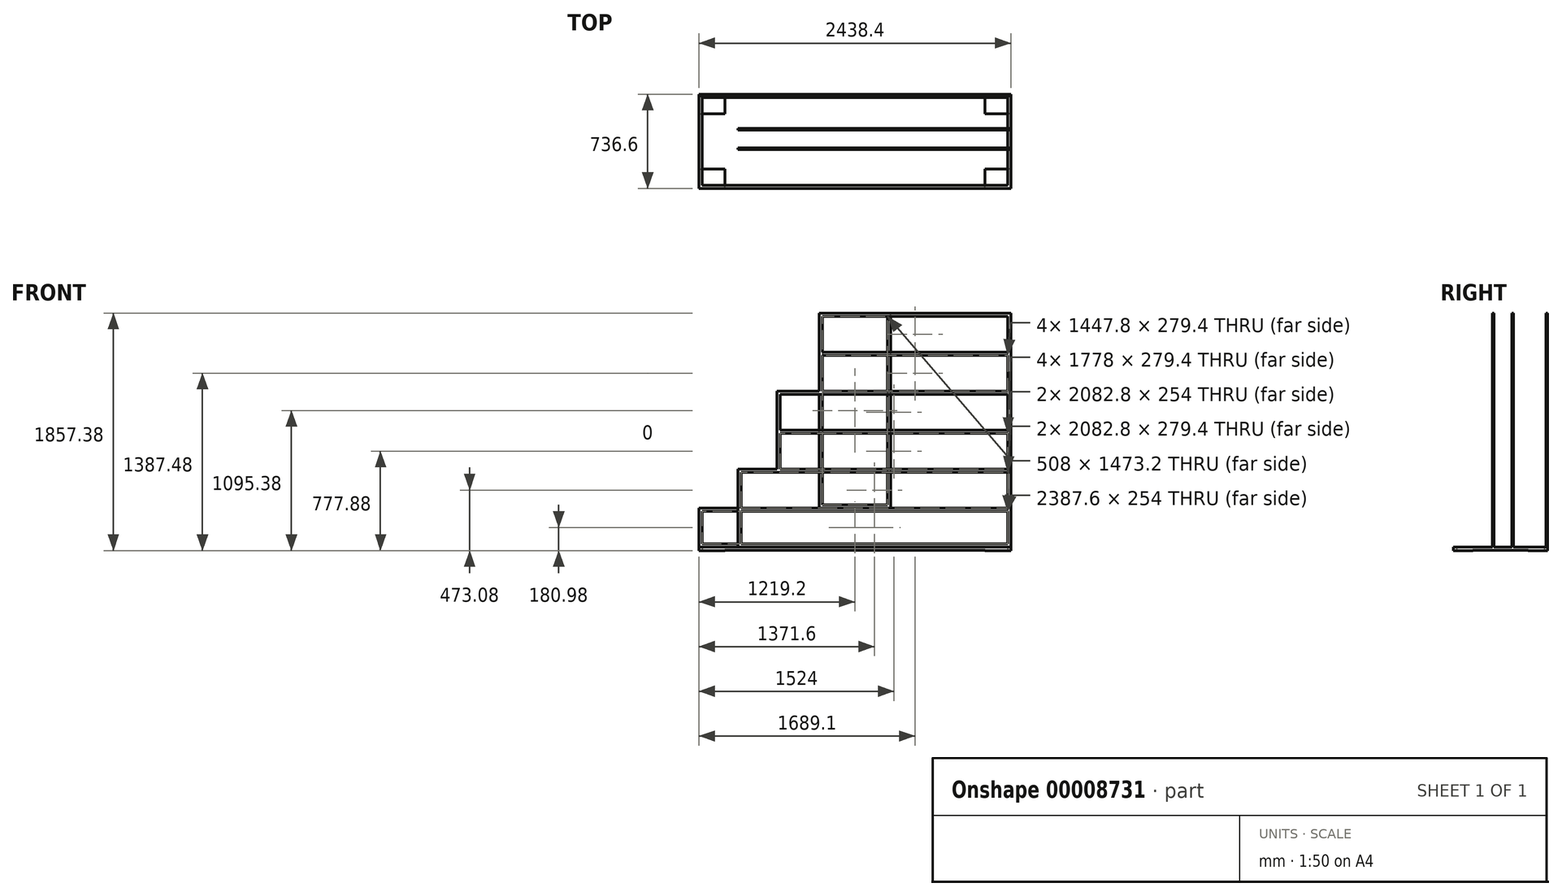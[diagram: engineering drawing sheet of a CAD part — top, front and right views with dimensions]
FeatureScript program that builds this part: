
annotation { "Feature Type Name" : "Feature", "Feature Type Description" : "" }
export const myFeature = defineFeature(function(context is Context, id is Id, definition is map)
    precondition{}
    {
        {
            var Q0;
            Q0=qCreatedBy(makeId("Top.planeOp"),FACE);
            var sketch = newSketch(context, id + "F0", { "sketchPlane" : qUnion([Q0])});
            skLineSegment(sketch, "E0.bottom", {"start": v(0, 0) * mm, "end": v(-2438.4, 0) * mm});
            skLineSegment(sketch, "E0.top", {"start": v(0, -736.6) * mm, "end": v(-2438.4, -736.6) * mm});
            skLineSegment(sketch, "E0.left", {"start": v(0, 0) * mm, "end": v(0, -736.6) * mm});
            skLineSegment(sketch, "E0.right", {"start": v(-2438.4, 0) * mm, "end": v(-2438.4, -736.6) * mm});
            skLineSegment(sketch, "E1.bottom", {"start": v(-25.4, -25.4) * mm, "end": v(-2413, -25.4) * mm});
            skLineSegment(sketch, "E1.top", {"start": v(-25.4, -711.2) * mm, "end": v(-2413, -711.2) * mm});
            skLineSegment(sketch, "E1.left", {"start": v(-25.4, -25.4) * mm, "end": v(-25.4, -711.2) * mm});
            skLineSegment(sketch, "E1.right", {"start": v(-2413, -25.4) * mm, "end": v(-2413, -711.2) * mm});
            skLineSegment(sketch, "E2.bottom", {"start": v(-2235.2, -25.4) * mm, "end": v(-2260.6, -25.4) * mm});
            skLineSegment(sketch, "E2.top", {"start": v(-2235.2, -711.2) * mm, "end": v(-2260.6, -711.2) * mm});
            skLineSegment(sketch, "E2.left", {"start": v(-2235.2, -25.4) * mm, "end": v(-2235.2, -711.2) * mm});
            skLineSegment(sketch, "E2.right", {"start": v(-2260.6, -25.4) * mm, "end": v(-2260.6, -711.2) * mm});
            skLineSegment(sketch, "E3.bottom", {"start": v(-203.2, -25.4) * mm, "end": v(-177.8, -25.4) * mm});
            skLineSegment(sketch, "E3.top", {"start": v(-203.2, -711.2) * mm, "end": v(-177.8, -711.2) * mm});
            skLineSegment(sketch, "E3.left", {"start": v(-203.2, -25.4) * mm, "end": v(-203.2, -711.2) * mm});
            skLineSegment(sketch, "E3.right", {"start": v(-177.8, -25.4) * mm, "end": v(-177.8, -711.2) * mm});
            skLineSegment(sketch, "E4.bottom", {"start": v(-1625.6, -25.4) * mm, "end": v(-1600.2, -25.4) * mm});
            skLineSegment(sketch, "E4.top", {"start": v(-1625.6, -711.2) * mm, "end": v(-1600.2, -711.2) * mm});
            skLineSegment(sketch, "E5.bottom", {"start": v(-1168.4, -25.4) * mm, "end": v(-1143, -25.4) * mm});
            skLineSegment(sketch, "E5.top", {"start": v(-1168.4, -711.2) * mm, "end": v(-1143, -711.2) * mm});
            skLineSegment(sketch, "E6.bottom", {"start": v(-838.2, -25.4) * mm, "end": v(-812.8, -25.4) * mm});
            skLineSegment(sketch, "E6.top", {"start": v(-838.2, -711.2) * mm, "end": v(-812.8, -711.2) * mm});
            skLineSegment(sketch, "E7.bottom", {"start": v(-1816.1, -25.4) * mm, "end": v(-1841.5, -25.4) * mm});
            skLineSegment(sketch, "E7.top", {"start": v(-1816.1, -711.2) * mm, "end": v(-1841.5, -711.2) * mm});
            skLineSegment(sketch, "E7.left", {"start": v(-1816.1, -25.4) * mm, "end": v(-1816.1, -711.2) * mm});
            skLineSegment(sketch, "E7.right", {"start": v(-1841.5, -25.4) * mm, "end": v(-1841.5, -711.2) * mm});
            skLineSegment(sketch, "E8.bottom", {"start": v(-1435.1, -25.4) * mm, "end": v(-1409.7, -25.4) * mm});
            skLineSegment(sketch, "E8.top", {"start": v(-1435.1, -711.2) * mm, "end": v(-1409.7, -711.2) * mm});
            skLineSegment(sketch, "E8.left", {"start": v(-1435.1, -25.4) * mm, "end": v(-1435.1, -711.2) * mm});
            skLineSegment(sketch, "E8.right", {"start": v(-1409.7, -25.4) * mm, "end": v(-1409.7, -711.2) * mm});
            skLineSegment(sketch, "E9.bottom", {"start": v(-1028.7, -25.4) * mm, "end": v(-1003.3, -25.4) * mm});
            skLineSegment(sketch, "E9.top", {"start": v(-1028.7, -711.2) * mm, "end": v(-1003.3, -711.2) * mm});
            skLineSegment(sketch, "E9.left", {"start": v(-1028.7, -25.4) * mm, "end": v(-1028.7, -711.2) * mm});
            skLineSegment(sketch, "E9.right", {"start": v(-1003.3, -25.4) * mm, "end": v(-1003.3, -711.2) * mm});
            skLineSegment(sketch, "E10.bottom", {"start": v(-622.3, -25.4) * mm, "end": v(-596.9, -25.4) * mm});
            skLineSegment(sketch, "E10.top", {"start": v(-622.3, -711.2) * mm, "end": v(-596.9, -711.2) * mm});
            skLineSegment(sketch, "E10.left", {"start": v(-622.3, -25.4) * mm, "end": v(-622.3, -711.2) * mm});
            skLineSegment(sketch, "E10.right", {"start": v(-596.9, -25.4) * mm, "end": v(-596.9, -711.2) * mm});
            skSolve(sketch);
        }
        {
            var Q0;
            Q0 = qSketchRegion(id + "F0", true);
            var Q1;
            Q1=makeQuery(id+"F0.imprint","IMPRINT",FACE,{"disambiguationData":[TD([[makeQuery(id+"F0.imprint","IMPRINT",EDGE,{"derivedFrom":sQuery(id+"F0.wireOp",EDGE,"E2.bottom")}),1.0]])]});
            var Q2;
            Q2=makeQuery(id+"F0.imprint","IMPRINT",FACE,{"disambiguationData":[TD([[makeQuery(id+"F0.imprint","IMPRINT",EDGE,{"derivedFrom":sQuery(id+"F0.wireOp",EDGE,"E7.bottom")}),1.0]])]});
            var Q3;
            Q3=makeQuery(id+"F0.imprint","IMPRINT",FACE,{"disambiguationData":[TD([[makeQuery(id+"F0.imprint","IMPRINT",EDGE,{"derivedFrom":sQuery(id+"F0.wireOp",EDGE,"E8.bottom")}),-1.0]])]});
            var Q4;
            Q4=makeQuery(id+"F0.imprint","IMPRINT",FACE,{"disambiguationData":[TD([[makeQuery(id+"F0.imprint","IMPRINT",EDGE,{"derivedFrom":sQuery(id+"F0.wireOp",EDGE,"E9.bottom")}),-1.0]])]});
            var Q5;
            Q5=makeQuery(id+"F0.imprint","IMPRINT",FACE,{"disambiguationData":[TD([[makeQuery(id+"F0.imprint","IMPRINT",EDGE,{"derivedFrom":sQuery(id+"F0.wireOp",EDGE,"E10.bottom")}),-1.0]])]});
            var Q6;
            Q6=makeQuery(id+"F0.imprint","IMPRINT",FACE,{"disambiguationData":[TD([[makeQuery(id+"F0.imprint","IMPRINT",EDGE,{"derivedFrom":sQuery(id+"F0.wireOp",EDGE,"E3.bottom")}),-1.0]])]});
            extrude(context, id + "F1", {"entities" : qUnion([Q0, Q1, Q2, Q3, Q4, Q5, Q6]), "depth" : 25.4 * mm});
        }
        {
            var Q0;
            Q0=makeQuery(id+"F1.opExtrude","CAP_FACE",FACE,{"disambiguationData":[OSD([sQuery(id+"F0.wireOp",EDGE,"E0.bottom"),sQuery(id+"F0.wireOp",EDGE,"E0.top"),sQuery(id+"F0.wireOp",EDGE,"E0.left"),sQuery(id+"F0.wireOp",EDGE,"E0.right"),sQuery(id+"F0.wireOp",EDGE,"E1.bottom"),sQuery(id+"F0.wireOp",EDGE,"E1.top"),sQuery(id+"F0.wireOp",EDGE,"E1.left"),sQuery(id+"F0.wireOp",EDGE,"E1.right"),sQuery(id+"F0.wireOp",EDGE,"E2.left"),sQuery(id+"F0.wireOp",EDGE,"E2.right"),sQuery(id+"F0.wireOp",EDGE,"E3.left"),sQuery(id+"F0.wireOp",EDGE,"E3.right"),sQuery(id+"F0.wireOp",EDGE,"E4.bottom"),sQuery(id+"F0.wireOp",EDGE,"E4.top"),sQuery(id+"F0.wireOp",EDGE,"E5.bottom"),sQuery(id+"F0.wireOp",EDGE,"E5.top"),sQuery(id+"F0.wireOp",EDGE,"E6.bottom"),sQuery(id+"F0.wireOp",EDGE,"E6.top"),sQuery(id+"F0.wireOp",EDGE,"E7.left"),sQuery(id+"F0.wireOp",EDGE,"E7.right"),sQuery(id+"F0.wireOp",EDGE,"E8.left"),sQuery(id+"F0.wireOp",EDGE,"E8.right"),sQuery(id+"F0.wireOp",EDGE,"E9.left"),sQuery(id+"F0.wireOp",EDGE,"E9.right"),sQuery(id+"F0.wireOp",EDGE,"E10.left"),sQuery(id+"F0.wireOp",EDGE,"E10.right")])],"isStart":true});
            var sketch = newSketch(context, id + "F2", { "sketchPlane" : qUnion([Q0])});
            skLineSegment(sketch, "E11.bottom", {"start": v(-2438.4, 736.6) * mm, "end": v(-2235.2, 736.6) * mm});
            skLineSegment(sketch, "E11.top", {"start": v(-2438.4, 584.2) * mm, "end": v(-2235.2, 584.2) * mm});
            skLineSegment(sketch, "E11.left", {"start": v(-2438.4, 736.6) * mm, "end": v(-2438.4, 584.2) * mm});
            skLineSegment(sketch, "E11.right", {"start": v(-2235.2, 736.6) * mm, "end": v(-2235.2, 584.2) * mm});
            skLineSegment(sketch, "E12.bottom", {"start": v(-2438.4, 0) * mm, "end": v(-2235.2, 0) * mm});
            skLineSegment(sketch, "E12.top", {"start": v(-2438.4, 152.4) * mm, "end": v(-2235.2, 152.4) * mm});
            skLineSegment(sketch, "E12.left", {"start": v(-2438.4, 0) * mm, "end": v(-2438.4, 152.4) * mm});
            skLineSegment(sketch, "E12.right", {"start": v(-2235.2, 0) * mm, "end": v(-2235.2, 152.4) * mm});
            skLineSegment(sketch, "E13.bottom", {"start": v(0, 736.6) * mm, "end": v(-203.2, 736.6) * mm});
            skLineSegment(sketch, "E13.top", {"start": v(0, 584.2) * mm, "end": v(-203.2, 584.2) * mm});
            skLineSegment(sketch, "E13.left", {"start": v(0, 736.6) * mm, "end": v(0, 584.2) * mm});
            skLineSegment(sketch, "E13.right", {"start": v(-203.2, 736.6) * mm, "end": v(-203.2, 584.2) * mm});
            skLineSegment(sketch, "E14.bottom", {"start": v(0, 0) * mm, "end": v(-203.2, 0) * mm});
            skLineSegment(sketch, "E14.top", {"start": v(0, 152.4) * mm, "end": v(-203.2, 152.4) * mm});
            skLineSegment(sketch, "E14.left", {"start": v(0, 0) * mm, "end": v(0, 152.4) * mm});
            skLineSegment(sketch, "E14.right", {"start": v(-203.2, 0) * mm, "end": v(-203.2, 152.4) * mm});
            skSolve(sketch);
        }
        {
            var Q0;
            Q0 = qSketchRegion(id + "F2", true);
            extrude(context, id + "F3", {"entities" : qUnion([Q0]), "operationType" : NewBodyOperationType.ADD, "depth" : 3.17 * mm});
        }
        {
            var Q0;
            Q0=makeQuery(id+"F3.boolean.opBoolean","MERGE",FACE,{"derivedFrom":[makeQuery(id+"F1.opExtrude","SWEPT_FACE",FACE,{"disambiguationData":[OSD([sQuery(id+"F0.wireOp",EDGE,"E0.bottom")])]}),makeQuery(id+"F3.opExtrude","SWEPT_FACE",FACE,{"disambiguationData":[OSD([sQuery(id+"F2.wireOp",EDGE,"E12.bottom")])]}),makeQuery(id+"F3.opExtrude","SWEPT_FACE",FACE,{"disambiguationData":[OSD([sQuery(id+"F2.wireOp",EDGE,"E14.bottom")])]})]});
            var sketch = newSketch(context, id + "F4", { "sketchPlane" : qUnion([Q0])});
            skLineSegment(sketch, "E15.bottom", {"start": v(0, 25.4) * mm, "end": v(2438.4, 25.4) * mm});
            skLineSegment(sketch, "E15.top", {"start": v(0, 330.2) * mm, "end": v(2438.4, 330.2) * mm});
            skLineSegment(sketch, "E15.left", {"start": v(0, 25.4) * mm, "end": v(0, 330.2) * mm});
            skLineSegment(sketch, "E15.right", {"start": v(2438.4, 25.4) * mm, "end": v(2438.4, 330.2) * mm});
            skLineSegment(sketch, "E16.bottom", {"start": v(939.8, 330.2) * mm, "end": v(1498.6, 330.2) * mm});
            skLineSegment(sketch, "E16.top", {"start": v(939.8, 1854.2) * mm, "end": v(1498.6, 1854.2) * mm});
            skLineSegment(sketch, "E16.left", {"start": v(939.8, 330.2) * mm, "end": v(939.8, 1854.2) * mm});
            skLineSegment(sketch, "E16.right", {"start": v(1498.6, 330.2) * mm, "end": v(1498.6, 1854.2) * mm});
            skLineSegment(sketch, "E17.bottom", {"start": v(965.2, 1828.8) * mm, "end": v(1473.2, 1828.8) * mm});
            skLineSegment(sketch, "E17.top", {"start": v(965.2, 355.6) * mm, "end": v(1473.2, 355.6) * mm});
            skLineSegment(sketch, "E17.left", {"start": v(965.2, 1828.8) * mm, "end": v(965.2, 355.6) * mm});
            skLineSegment(sketch, "E17.right", {"start": v(1473.2, 1828.8) * mm, "end": v(1473.2, 355.6) * mm});
            skLineSegment(sketch, "E18.bottom", {"start": v(25.4, 304.8) * mm, "end": v(2413, 304.8) * mm});
            skLineSegment(sketch, "E18.top", {"start": v(25.4, 50.8) * mm, "end": v(2413, 50.8) * mm});
            skLineSegment(sketch, "E18.left", {"start": v(25.4, 304.8) * mm, "end": v(25.4, 50.8) * mm});
            skLineSegment(sketch, "E18.right", {"start": v(2413, 304.8) * mm, "end": v(2413, 50.8) * mm});
            skLineSegment(sketch, "E19.bottom", {"start": v(635, 304.8) * mm, "end": v(660.4, 304.8) * mm});
            skLineSegment(sketch, "E19.top", {"start": v(635, 50.8) * mm, "end": v(660.4, 50.8) * mm});
            skLineSegment(sketch, "E19.left", {"start": v(635, 304.8) * mm, "end": v(635, 50.8) * mm});
            skLineSegment(sketch, "E19.right", {"start": v(660.4, 304.8) * mm, "end": v(660.4, 50.8) * mm});
            skLineSegment(sketch, "E20.bottom", {"start": v(1778, 304.8) * mm, "end": v(1803.4, 304.8) * mm});
            skLineSegment(sketch, "E20.top", {"start": v(1778, 50.8) * mm, "end": v(1803.4, 50.8) * mm});
            skLineSegment(sketch, "E20.left", {"start": v(1778, 304.8) * mm, "end": v(1778, 50.8) * mm});
            skLineSegment(sketch, "E20.right", {"start": v(1803.4, 304.8) * mm, "end": v(1803.4, 50.8) * mm});
            skSolve(sketch);
        }
        {
            var Q0;
            Q0 = qSketchRegion(id + "F4", true);
            var Q1;
            Q1=makeQuery(id+"F4.imprint","IMPRINT",FACE,{"disambiguationData":[TD([[makeQuery(id+"F4.imprint","IMPRINT",EDGE,{"derivedFrom":sQuery(id+"F4.wireOp",EDGE,"E20.bottom")}),-1.0]])]});
            var Q2;
            Q2=makeQuery(id+"F4.imprint","IMPRINT",FACE,{"disambiguationData":[TD([[makeQuery(id+"F4.imprint","IMPRINT",EDGE,{"derivedFrom":sQuery(id+"F4.wireOp",EDGE,"E19.bottom")}),-1.0]])]});
            extrude(context, id + "F5", {"entities" : qUnion([Q0, Q1, Q2]), "oppositeDirection" : true, "depth" : 12.7 * mm});
        }
        {
            var Q0;
            Q0=makeQuery(id+"F5.opExtrude","CAP_FACE",FACE,{"disambiguationData":[OSD([sQuery(id+"F4.wireOp",EDGE,"E15.bottom"),sQuery(id+"F4.wireOp",EDGE,"E15.top"),sQuery(id+"F4.wireOp",EDGE,"E15.left"),sQuery(id+"F4.wireOp",EDGE,"E15.right"),sQuery(id+"F4.wireOp",EDGE,"E16.top"),sQuery(id+"F4.wireOp",EDGE,"E16.left"),sQuery(id+"F4.wireOp",EDGE,"E16.right"),sQuery(id+"F4.wireOp",EDGE,"E17.bottom"),sQuery(id+"F4.wireOp",EDGE,"E17.top"),sQuery(id+"F4.wireOp",EDGE,"E17.left"),sQuery(id+"F4.wireOp",EDGE,"E17.right"),sQuery(id+"F4.wireOp",EDGE,"E18.bottom"),sQuery(id+"F4.wireOp",EDGE,"E18.top"),sQuery(id+"F4.wireOp",EDGE,"E18.left"),sQuery(id+"F4.wireOp",EDGE,"E18.right"),sQuery(id+"F4.wireOp",EDGE,"E19.left"),sQuery(id+"F4.wireOp",EDGE,"E19.right"),sQuery(id+"F4.wireOp",EDGE,"E20.left"),sQuery(id+"F4.wireOp",EDGE,"E20.right")])],"isStart":false});
            cPlane(context, id + "F6", {"entities" : qUnion([Q0]), "cplaneType" : CPlaneType.OFFSET, "offset" : 254 * mm, "width" : 152.4 * mm, "height" : 152.4 * mm});
        }
        {
            var Q0;
            Q0=qCreatedBy(id+"F6.planeOp",FACE);
            var sketch = newSketch(context, id + "F7", { "sketchPlane" : qUnion([Q0])});
            skPoint(sketch, "E21.0", {"position": v(-2438.4, 25.4) * mm});
            skPoint(sketch, "E22.0", {"position": v(0, 25.4) * mm});
            skLineSegment(sketch, "E23.0", {"start": v(-939.8, 1854.2) * mm, "end": v(-1498.6, 1854.2) * mm});
            skLineSegment(sketch, "E24.bottom", {"start": v(0, 25.4) * mm, "end": v(-2133.6, 25.4) * mm});
            skLineSegment(sketch, "E24.top", {"start": v(0, 330.2) * mm, "end": v(-2133.6, 330.2) * mm});
            skLineSegment(sketch, "E24.left", {"start": v(0, 25.4) * mm, "end": v(0, 330.2) * mm});
            skLineSegment(sketch, "E24.right", {"start": v(-2133.6, 25.4) * mm, "end": v(-2133.6, 330.2) * mm});
            skLineSegment(sketch, "E25.top", {"start": v(0, 635) * mm, "end": v(-2133.6, 635) * mm});
            skLineSegment(sketch, "E25.left", {"start": v(0, 330.2) * mm, "end": v(0, 635) * mm});
            skLineSegment(sketch, "E25.right", {"start": v(-2133.6, 330.2) * mm, "end": v(-2133.6, 635) * mm});
            skLineSegment(sketch, "E26.bottom", {"start": v(0, 635) * mm, "end": v(-1828.8, 635) * mm});
            skLineSegment(sketch, "E26.top", {"start": v(0, 939.8) * mm, "end": v(-1828.8, 939.8) * mm});
            skLineSegment(sketch, "E26.left", {"start": v(0, 635) * mm, "end": v(0, 939.8) * mm});
            skLineSegment(sketch, "E26.right", {"start": v(-1828.8, 635) * mm, "end": v(-1828.8, 939.8) * mm});
            skLineSegment(sketch, "E27.top", {"start": v(0, 1244.6) * mm, "end": v(-1828.8, 1244.6) * mm});
            skLineSegment(sketch, "E27.left", {"start": v(0, 939.8) * mm, "end": v(0, 1244.6) * mm});
            skLineSegment(sketch, "E27.right", {"start": v(-1828.8, 939.8) * mm, "end": v(-1828.8, 1244.6) * mm});
            skLineSegment(sketch, "E28.bottom", {"start": v(0, 1244.6) * mm, "end": v(-1498.6, 1244.6) * mm});
            skLineSegment(sketch, "E28.top", {"start": v(0, 1549.4) * mm, "end": v(-1498.6, 1549.4) * mm});
            skLineSegment(sketch, "E28.left", {"start": v(0, 1244.6) * mm, "end": v(0, 1549.4) * mm});
            skLineSegment(sketch, "E28.right", {"start": v(-1498.6, 1244.6) * mm, "end": v(-1498.6, 1549.4) * mm});
            skLineSegment(sketch, "E29.top", {"start": v(0, 1854.2) * mm, "end": v(-1498.6, 1854.2) * mm});
            skLineSegment(sketch, "E29.left", {"start": v(0, 1549.4) * mm, "end": v(0, 1854.2) * mm});
            skLineSegment(sketch, "E29.right", {"start": v(-1498.6, 1549.4) * mm, "end": v(-1498.6, 1854.2) * mm});
            skLineSegment(sketch, "E30.bottom", {"start": v(-2108.2, 25.4) * mm, "end": v(-25.4, 25.4) * mm});
            skLineSegment(sketch, "E30.top", {"start": v(-2108.2, 304.8) * mm, "end": v(-25.4, 304.8) * mm});
            skLineSegment(sketch, "E30.left", {"start": v(-2108.2, 25.4) * mm, "end": v(-2108.2, 304.8) * mm});
            skLineSegment(sketch, "E30.right", {"start": v(-25.4, 25.4) * mm, "end": v(-25.4, 304.8) * mm});
            skLineSegment(sketch, "E31.bottom", {"start": v(-2108.2, 330.2) * mm, "end": v(-25.4, 330.2) * mm});
            skLineSegment(sketch, "E31.top", {"start": v(-2108.2, 609.6) * mm, "end": v(-25.4, 609.6) * mm});
            skLineSegment(sketch, "E31.left", {"start": v(-2108.2, 330.2) * mm, "end": v(-2108.2, 609.6) * mm});
            skLineSegment(sketch, "E31.right", {"start": v(-25.4, 330.2) * mm, "end": v(-25.4, 609.6) * mm});
            skLineSegment(sketch, "E32.bottom", {"start": v(-1803.4, 635) * mm, "end": v(-25.4, 635) * mm});
            skLineSegment(sketch, "E32.top", {"start": v(-1803.4, 914.4) * mm, "end": v(-25.4, 914.4) * mm});
            skLineSegment(sketch, "E32.left", {"start": v(-1803.4, 635) * mm, "end": v(-1803.4, 914.4) * mm});
            skLineSegment(sketch, "E32.right", {"start": v(-25.4, 635) * mm, "end": v(-25.4, 914.4) * mm});
            skLineSegment(sketch, "E33.bottom", {"start": v(-1803.4, 939.8) * mm, "end": v(-25.4, 939.8) * mm});
            skLineSegment(sketch, "E33.top", {"start": v(-1803.4, 1219.2) * mm, "end": v(-25.4, 1219.2) * mm});
            skLineSegment(sketch, "E33.left", {"start": v(-1803.4, 939.8) * mm, "end": v(-1803.4, 1219.2) * mm});
            skLineSegment(sketch, "E33.right", {"start": v(-25.4, 939.8) * mm, "end": v(-25.4, 1219.2) * mm});
            skLineSegment(sketch, "E34.bottom", {"start": v(-1473.2, 1244.6) * mm, "end": v(-25.4, 1244.6) * mm});
            skLineSegment(sketch, "E34.top", {"start": v(-1473.2, 1524) * mm, "end": v(-25.4, 1524) * mm});
            skLineSegment(sketch, "E34.left", {"start": v(-1473.2, 1244.6) * mm, "end": v(-1473.2, 1524) * mm});
            skLineSegment(sketch, "E34.right", {"start": v(-25.4, 1244.6) * mm, "end": v(-25.4, 1524) * mm});
            skLineSegment(sketch, "E35.bottom", {"start": v(-1473.2, 1549.4) * mm, "end": v(-25.4, 1549.4) * mm});
            skLineSegment(sketch, "E35.top", {"start": v(-1473.2, 1828.8) * mm, "end": v(-25.4, 1828.8) * mm});
            skLineSegment(sketch, "E35.left", {"start": v(-1473.2, 1549.4) * mm, "end": v(-1473.2, 1828.8) * mm});
            skLineSegment(sketch, "E35.right", {"start": v(-25.4, 1549.4) * mm, "end": v(-25.4, 1828.8) * mm});
            skLineSegment(sketch, "E36.bottom", {"start": v(-2108.2, 50.8) * mm, "end": v(-25.4, 50.8) * mm});
            skLineSegment(sketch, "E36.left", {"start": v(-2108.2, 50.8) * mm, "end": v(-2108.2, 25.4) * mm});
            skLineSegment(sketch, "E36.right", {"start": v(-25.4, 50.8) * mm, "end": v(-25.4, 25.4) * mm});
            skSolve(sketch);
        }
        {
            var Q0;
            {var subQ3=sQuery(id+"F7.wireOp",EDGE,"E29.left");Q0=makeQuery(id+"F7.imprint","IMPRINT",FACE,{"disambiguationData":[TD([[makeQuery(id+"F7.imprint","IMPRINT",EDGE,{"derivedFrom":subQ3}),1.0]])]});}
            var Q1;
            {var subQ5=sQuery(id+"F7.wireOp",EDGE,"E24.left");Q1=makeQuery(id+"F7.imprint","IMPRINT",FACE,{"disambiguationData":[TD([[makeQuery(id+"F7.imprint","IMPRINT",EDGE,{"derivedFrom":subQ5}),1.0]])]});}
            var Q2;
            {var subQ5=sQuery(id+"F7.wireOp",EDGE,"E25.top");Q2=makeQuery(id+"F7.imprint","IMPRINT",FACE,{"disambiguationData":[TD([[makeQuery(id+"F7.imprint","IMPRINT",EDGE,{"derivedFrom":subQ5}),1.0]])]});}
            var Q3;
            {var subQ5=sQuery(id+"F7.wireOp",EDGE,"E26.left");Q3=makeQuery(id+"F7.imprint","IMPRINT",FACE,{"disambiguationData":[TD([[makeQuery(id+"F7.imprint","IMPRINT",EDGE,{"derivedFrom":subQ5}),1.0]])]});}
            var Q4;
            {var subQ4=sQuery(id+"F7.wireOp",EDGE,"E27.top");Q4=makeQuery(id+"F7.imprint","IMPRINT",FACE,{"disambiguationData":[TD([[makeQuery(id+"F7.imprint","IMPRINT",EDGE,{"derivedFrom":subQ4}),1.0]])]});}
            var Q5;
            {var subQ4=sQuery(id+"F7.wireOp",EDGE,"E28.left");Q5=makeQuery(id+"F7.imprint","IMPRINT",FACE,{"disambiguationData":[TD([[makeQuery(id+"F7.imprint","IMPRINT",EDGE,{"derivedFrom":subQ4}),1.0]])]});}
            var Q6;
            Q6=makeQuery(id+"F7.imprint","IMPRINT",FACE,{"disambiguationData":[TD([[makeQuery(id+"F7.imprint","IMPRINT",EDGE,{"derivedFrom":sQuery(id+"F7.wireOp",EDGE,"E36.bottom")}),-1.0]])]});
            extrude(context, id + "F8", {"entities" : qUnion([Q0, Q1, Q2, Q3, Q4, Q5, Q6]), "operationType" : NewBodyOperationType.ADD, "depth" : 12.7 * mm});
        }
        {
            var Q0;
            Q0=qCreatedBy(id+"F6.planeOp",FACE);
            cPlane(context, id + "F9", {"entities" : qUnion([Q0]), "cplaneType" : CPlaneType.OFFSET, "offset" : 152.4 * mm, "width" : 152.4 * mm, "height" : 152.4 * mm});
        }
        {
            var Q0;
            Q0=qCreatedBy(id+"F9.planeOp",FACE);
            var sketch = newSketch(context, id + "F10", { "sketchPlane" : qUnion([Q0])});
            skPoint(sketch, "E37.0", {"position": v(-1499.99, -826.65) * mm});
            skPoint(sketch, "E38.0", {"position": v(0, 25.4) * mm});
            skLineSegment(sketch, "E39.0", {"start": v(-1.39, 1002.15) * mm, "end": v(-560.19, 1002.15) * mm});
            skLineSegment(sketch, "E40.bottom", {"start": v(0, 25.4) * mm, "end": v(-2133.6, 25.4) * mm});
            skLineSegment(sketch, "E40.top", {"start": v(0, 330.2) * mm, "end": v(-2133.6, 330.2) * mm});
            skLineSegment(sketch, "E40.left", {"start": v(0, 25.4) * mm, "end": v(0, 330.2) * mm});
            skLineSegment(sketch, "E40.right", {"start": v(-2133.6, 25.4) * mm, "end": v(-2133.6, 330.2) * mm});
            skLineSegment(sketch, "E41.top", {"start": v(0, 635) * mm, "end": v(-2133.6, 635) * mm});
            skLineSegment(sketch, "E41.left", {"start": v(0, 330.2) * mm, "end": v(0, 635) * mm});
            skLineSegment(sketch, "E41.right", {"start": v(-2133.6, 330.2) * mm, "end": v(-2133.6, 635) * mm});
            skLineSegment(sketch, "E42.bottom", {"start": v(0, 635) * mm, "end": v(-1828.8, 635) * mm});
            skLineSegment(sketch, "E42.top", {"start": v(0, 939.8) * mm, "end": v(-1828.8, 939.8) * mm});
            skLineSegment(sketch, "E42.left", {"start": v(0, 635) * mm, "end": v(0, 939.8) * mm});
            skLineSegment(sketch, "E42.right", {"start": v(-1828.8, 635) * mm, "end": v(-1828.8, 939.8) * mm});
            skLineSegment(sketch, "E43.top", {"start": v(0, 1244.6) * mm, "end": v(-1828.8, 1244.6) * mm});
            skLineSegment(sketch, "E43.left", {"start": v(0, 939.8) * mm, "end": v(0, 1244.6) * mm});
            skLineSegment(sketch, "E43.right", {"start": v(-1828.8, 939.8) * mm, "end": v(-1828.8, 1244.6) * mm});
            skLineSegment(sketch, "E44.bottom", {"start": v(0, 1244.6) * mm, "end": v(-1498.6, 1244.6) * mm});
            skLineSegment(sketch, "E44.top", {"start": v(0, 1549.4) * mm, "end": v(-1498.6, 1549.4) * mm});
            skLineSegment(sketch, "E44.left", {"start": v(0, 1244.6) * mm, "end": v(0, 1549.4) * mm});
            skLineSegment(sketch, "E44.right", {"start": v(-1498.6, 1244.6) * mm, "end": v(-1498.6, 1549.4) * mm});
            skLineSegment(sketch, "E45.top", {"start": v(0, 1854.2) * mm, "end": v(-1498.6, 1854.2) * mm});
            skLineSegment(sketch, "E45.left", {"start": v(0, 1549.4) * mm, "end": v(0, 1854.2) * mm});
            skLineSegment(sketch, "E45.right", {"start": v(-1498.6, 1549.4) * mm, "end": v(-1498.6, 1854.2) * mm});
            skLineSegment(sketch, "E46.bottom", {"start": v(-2108.2, 25.4) * mm, "end": v(-25.4, 25.4) * mm});
            skLineSegment(sketch, "E46.top", {"start": v(-2108.2, 304.8) * mm, "end": v(-25.4, 304.8) * mm});
            skLineSegment(sketch, "E46.left", {"start": v(-2108.2, 25.4) * mm, "end": v(-2108.2, 304.8) * mm});
            skLineSegment(sketch, "E46.right", {"start": v(-25.4, 25.4) * mm, "end": v(-25.4, 304.8) * mm});
            skLineSegment(sketch, "E47.bottom", {"start": v(-2108.2, 330.2) * mm, "end": v(-25.4, 330.2) * mm});
            skLineSegment(sketch, "E47.top", {"start": v(-2108.2, 609.6) * mm, "end": v(-25.4, 609.6) * mm});
            skLineSegment(sketch, "E47.left", {"start": v(-2108.2, 330.2) * mm, "end": v(-2108.2, 609.6) * mm});
            skLineSegment(sketch, "E47.right", {"start": v(-25.4, 330.2) * mm, "end": v(-25.4, 609.6) * mm});
            skLineSegment(sketch, "E48.bottom", {"start": v(-1803.4, 635) * mm, "end": v(-25.4, 635) * mm});
            skLineSegment(sketch, "E48.top", {"start": v(-1803.4, 914.4) * mm, "end": v(-25.4, 914.4) * mm});
            skLineSegment(sketch, "E48.left", {"start": v(-1803.4, 635) * mm, "end": v(-1803.4, 914.4) * mm});
            skLineSegment(sketch, "E48.right", {"start": v(-25.4, 635) * mm, "end": v(-25.4, 914.4) * mm});
            skLineSegment(sketch, "E49.bottom", {"start": v(-1803.4, 939.8) * mm, "end": v(-25.4, 939.8) * mm});
            skLineSegment(sketch, "E49.top", {"start": v(-1803.4, 1219.2) * mm, "end": v(-25.4, 1219.2) * mm});
            skLineSegment(sketch, "E49.left", {"start": v(-1803.4, 939.8) * mm, "end": v(-1803.4, 1219.2) * mm});
            skLineSegment(sketch, "E49.right", {"start": v(-25.4, 939.8) * mm, "end": v(-25.4, 1219.2) * mm});
            skLineSegment(sketch, "E50.bottom", {"start": v(-1473.2, 1244.6) * mm, "end": v(-25.4, 1244.6) * mm});
            skLineSegment(sketch, "E50.top", {"start": v(-1473.2, 1524) * mm, "end": v(-25.4, 1524) * mm});
            skLineSegment(sketch, "E50.left", {"start": v(-1473.2, 1244.6) * mm, "end": v(-1473.2, 1524) * mm});
            skLineSegment(sketch, "E50.right", {"start": v(-25.4, 1244.6) * mm, "end": v(-25.4, 1524) * mm});
            skLineSegment(sketch, "E51.bottom", {"start": v(-1473.2, 1549.4) * mm, "end": v(-25.4, 1549.4) * mm});
            skLineSegment(sketch, "E51.top", {"start": v(-1473.2, 1828.8) * mm, "end": v(-25.4, 1828.8) * mm});
            skLineSegment(sketch, "E51.left", {"start": v(-1473.2, 1549.4) * mm, "end": v(-1473.2, 1828.8) * mm});
            skLineSegment(sketch, "E51.right", {"start": v(-25.4, 1549.4) * mm, "end": v(-25.4, 1828.8) * mm});
            skLineSegment(sketch, "E52.bottom", {"start": v(-2108.2, 50.8) * mm, "end": v(-25.4, 50.8) * mm});
            skLineSegment(sketch, "E52.left", {"start": v(-2108.2, 50.8) * mm, "end": v(-2108.2, 25.4) * mm});
            skLineSegment(sketch, "E52.right", {"start": v(-25.4, 50.8) * mm, "end": v(-25.4, 25.4) * mm});
            skLineSegment(sketch, "E53.0", {"start": v(-1498.6, 1244.6) * mm, "end": v(-1498.6, 1854.2) * mm});
            skSolve(sketch);
        }
        {
            var Q0;
            Q0 = qSketchRegion(id + "F10", true);
            extrude(context, id + "F11", {"entities" : qUnion([Q0]), "operationType" : NewBodyOperationType.ADD, "depth" : 12.7 * mm});
        }
    });
